# Revit family: Hurricane Resiliance Overhead Concealed Fixed Sidelite Bi-part Full Impact_GOTOVO
name_source: partatom
category: Doors
revit_build: Autodesk Revit Architecture 2014 (Build: 20130308_1515(x64)
units: mm (PartAtom-declared; Revit-internal decimal feet)

## types (1)
- Hurricane Resiliance Overhead Concealed Fixed Sidelite Bi-part Full Impact_GOTOVO
    Analytic Construction = <None>
    BIMobject category = Sliding Doors
    Bottom Profile Height = SL500 Fixed Panel : 0'  4"
    Bottom Profile Option 01 = SL500 Fixed Panel : 0'  4"
    Bottom Profile Option 02 = SL500 Fixed Panel : 0'  7"
    Bottom Profile Option 03 = SL500 Fixed Panel : 0'  10"
    Bottom Profile Option 04 = SL500 Fixed Panel : 0'  12"
    Brass Polished Finish = Brass, Polished
    Brass Satin Finish = Brass, Satin
    Clear Anodized = Clear Anodized
    Dark Bronze Anodized = Dark Bronze Anodized
    Date of publishing = 2015-02-23
    Depth = 0.00
    Dimensions Overconstraint = No
    Edition number = 1
    Frame Material = Clear Anodized
    Function = Interior
    Gap = 0' - 0 1/4"
    Glass = Glass
    Height = 7' - 5 3/4"
    IFC Classification = Door
    Leaf Height = 6' - 9 1/16"
    Leaf Width = 3' - 6 11/16"
    Manufacturer name = Besam-North America
    Material main = Aluminium
    NBS Reference Code = 25-30-20-77
    NBS Reference Description = Sliding Doorset Systems
    Nominal height = 0.00
    Nominal width = 0.00
    Product SKU = Resilience_OHC_FI
    Product data url = http://besam-na.bimobject.com
    Product family = Sliding
    Product group = Hurricane Resistant
    QR code = http://besam-na.bimobject.com
    Rough Height = 7' - 6"
    Rough Width = 14' - 0 1/2"
    Rubber = Rubber, Black
    Stainless Steel Polished Finish = Stainless Steel, Polished
    Stainless Steel Satin Finish = Stainless Steel, Satin
    Thickness = 0' - 4 1/2"
    UNSPSC Code = 301715
    Uniclass 1.4 Code = L4133
    Uniclass 1.4 Description = Sliding
    Uniclass 2.0 Code = SS-25-30-20-77
    Uniclass 2.0 Description = Sliding Doorset Systems
    Wall Closure = By host
    Weight Net (Kg) = 0
    Width = 14' - 0"

## geometry (parser evidence)
native form markers: Blend x4, Sweep x22
no freeform markers — native parametric forms only
